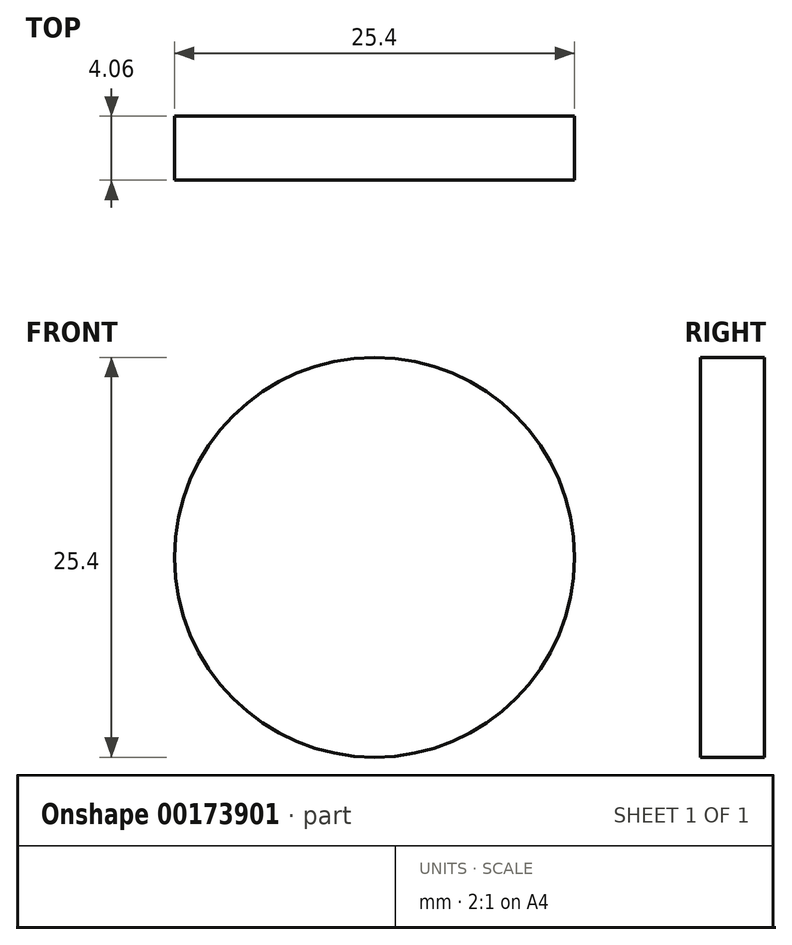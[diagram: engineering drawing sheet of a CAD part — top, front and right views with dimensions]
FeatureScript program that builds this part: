
annotation { "Feature Type Name" : "Feature", "Feature Type Description" : "" }
export const myFeature = defineFeature(function(context is Context, id is Id, definition is map)
    precondition{}
    {
        {
            var Q0;
            Q0=qCreatedBy(makeId("Front.planeOp"),FACE);
            var sketch = newSketch(context, id + "F0", { "sketchPlane" : qUnion([Q0])});
            skCircle(sketch, "E0", {"center": v(0, 0) * mm, "radius": 12.7 * mm});
            skSolve(sketch);
        }
        {
            var Q0;
            Q0=makeQuery(id+"F0.imprint","IMPRINT",FACE,{"disambiguationData":[TD([[makeQuery(id+"F0.imprint","IMPRINT",EDGE,{"derivedFrom":sQuery(id+"F0.wireOp",EDGE,"E0")}),1.0]])]});
            extrude(context, id + "F1", {"entities" : qUnion([Q0]), "depth" : 4.06 * mm});
        }
    });
